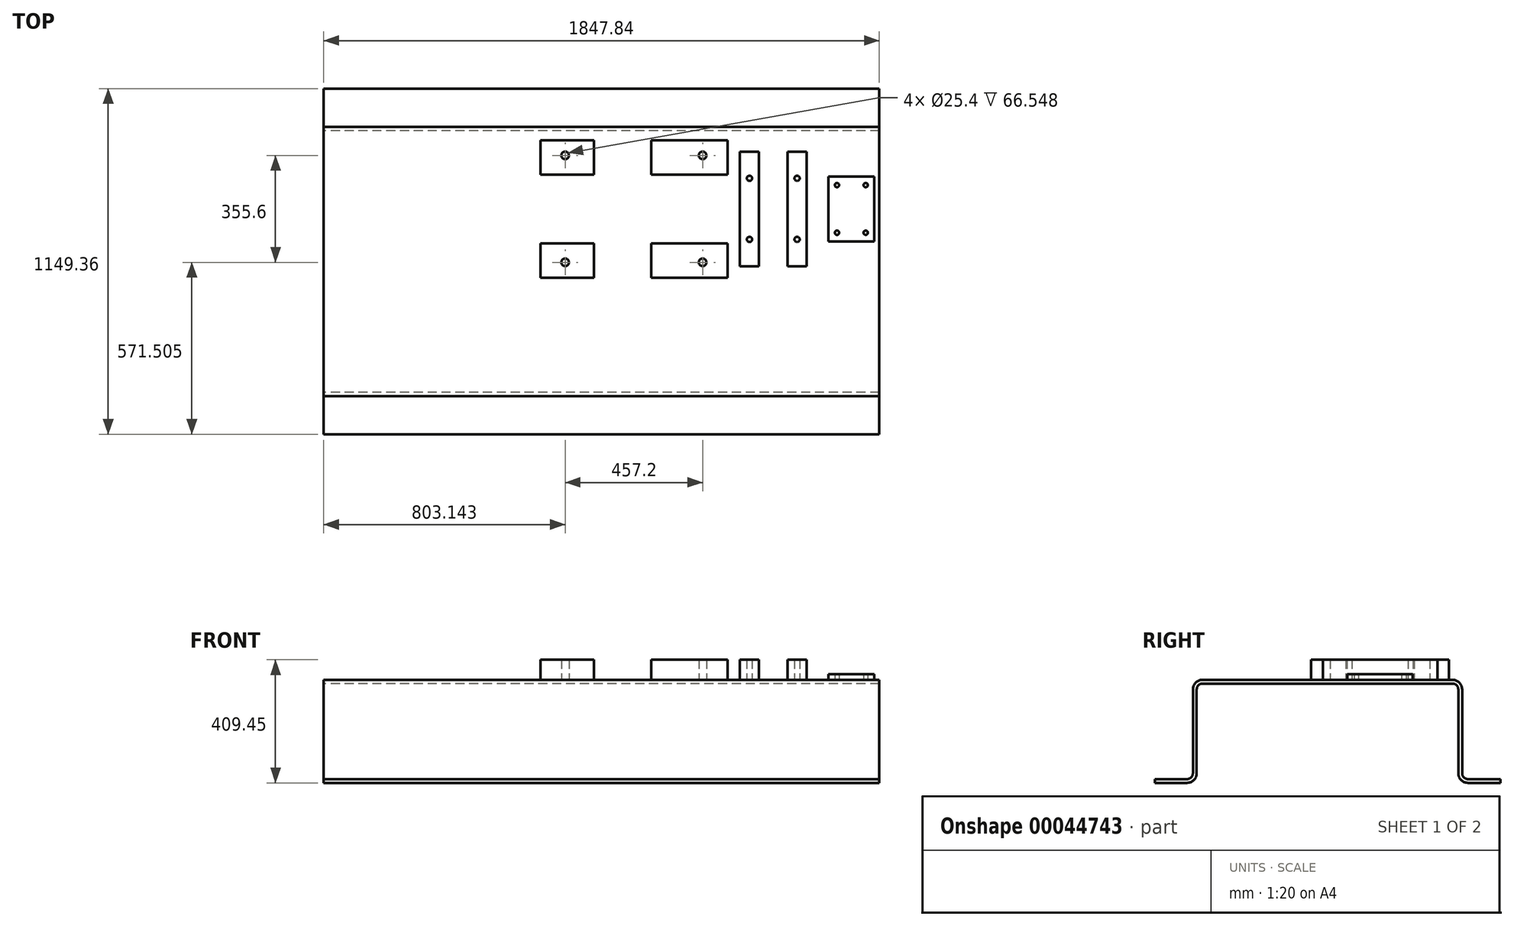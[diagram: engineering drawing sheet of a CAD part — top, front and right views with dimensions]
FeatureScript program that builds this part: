
annotation { "Feature Type Name" : "Feature", "Feature Type Description" : "" }
export const myFeature = defineFeature(function(context is Context, id is Id, definition is map)
    precondition{}
    {
        {
            var Q0;
            Q0=qCreatedBy(makeId("Right.planeOp"),FACE);
            var sketch = newSketch(context, id + "F0", { "sketchPlane" : qUnion([Q0])});
            skLineSegment(sketch, "E0.rect.bottom", {"start": v(-415.92, 171.45) * mm, "end": v(415.93, 171.45) * mm});
            skLineSegment(sketch, "E0.rect.top", {"start": v(-574.68, -171.45) * mm, "end": v(-466.73, -171.45) * mm});
            skLineSegment(sketch, "E0.rect.left", {"start": v(-447.68, 139.7) * mm, "end": v(-447.68, -139.7) * mm});
            skLineSegment(sketch, "E0.rect.right", {"start": v(447.68, 139.7) * mm, "end": v(447.68, -139.7) * mm});
            skPoint(sketch, "E0.rect.middle", {"position": v(0, 0) * mm});
            skLineSegment(sketch, "E1.0", {"start": v(-415.93, 158.75) * mm, "end": v(415.92, 158.75) * mm});
            skLineSegment(sketch, "E1.1", {"start": v(-434.98, 139.7) * mm, "end": v(-434.98, -139.7) * mm});
            skLineSegment(sketch, "E1.2", {"start": v(-574.68, -158.75) * mm, "end": v(-466.73, -158.75) * mm});
            skLineSegment(sketch, "E1.3", {"start": v(434.97, 139.7) * mm, "end": v(434.97, -139.7) * mm});
            skLineSegment(sketch, "E2.0", {"start": v(-574.68, -158.75) * mm, "end": v(-574.68, -171.45) * mm});
            skPoint(sketch, "E3.orphan", {"position": v(-447.68, -171.45) * mm});
            skLineSegment(sketch, "E4", {"start": v(0, 0) * mm, "end": v(0, 367.06) * mm, "construction": true});
            skLineSegment(sketch, "E5.MirrorCS", {"start": v(574.68, -158.75) * mm, "end": v(574.68, -171.45) * mm});
            skLineSegment(sketch, "E6.MirrorCS", {"start": v(574.68, -158.75) * mm, "end": v(466.73, -158.75) * mm});
            skPoint(sketch, "E7.MirrorP", {"position": v(447.68, -171.45) * mm});
            skLineSegment(sketch, "E8.MirrorCS", {"start": v(574.68, -171.45) * mm, "end": v(466.73, -171.45) * mm});
            skPoint(sketch, "E9.visualSharp", {"position": v(447.68, -158.75) * mm});
            skArc(sketch, "E9.filletArc", {"start": v(447.68, -139.7) * mm, "mid": v(453.25, -153.17) * mm, "end": v(466.73, -158.75) * mm});
            skPoint(sketch, "E10.visualSharp", {"position": v(434.98, 158.75) * mm});
            skArc(sketch, "E10.filletArc", {"start": v(434.97, 139.7) * mm, "mid": v(429.4, 153.17) * mm, "end": v(415.92, 158.75) * mm});
            skPoint(sketch, "E11.visualSharp", {"position": v(-434.98, 158.75) * mm});
            skArc(sketch, "E11.filletArc", {"start": v(-415.93, 158.75) * mm, "mid": v(-429.4, 153.17) * mm, "end": v(-434.98, 139.7) * mm});
            skPoint(sketch, "E12.visualSharp", {"position": v(-447.68, -158.75) * mm});
            skArc(sketch, "E12.filletArc", {"start": v(-466.73, -158.75) * mm, "mid": v(-453.25, -153.17) * mm, "end": v(-447.68, -139.7) * mm});
            skPoint(sketch, "E13.visualSharp", {"position": v(-434.98, -171.45) * mm});
            skArc(sketch, "E13.filletArc", {"start": v(-466.73, -171.45) * mm, "mid": v(-444.27, -162.15) * mm, "end": v(-434.98, -139.7) * mm});
            skPoint(sketch, "E14.visualSharp", {"position": v(-447.68, 171.45) * mm});
            skArc(sketch, "E14.filletArc", {"start": v(-415.92, 171.45) * mm, "mid": v(-438.38, 162.15) * mm, "end": v(-447.67, 139.7) * mm});
            skPoint(sketch, "E15.visualSharp", {"position": v(447.68, 171.45) * mm});
            skArc(sketch, "E15.filletArc", {"start": v(447.68, 139.7) * mm, "mid": v(438.38, 162.15) * mm, "end": v(415.93, 171.45) * mm});
            skPoint(sketch, "E16.visualSharp", {"position": v(434.97, -171.45) * mm});
            skArc(sketch, "E16.filletArc", {"start": v(434.98, -139.7) * mm, "mid": v(444.27, -162.15) * mm, "end": v(466.73, -171.45) * mm});
            skSolve(sketch);
        }
        {
            var Q0;
            Q0 = qSketchRegion(id + "F0", true);
            extrude(context, id + "F1", {"entities" : qUnion([Q0]), "endBound" : BoundingType.SYMMETRIC, "depth" : 1847.85 * mm});
        }
        {
            var Q0;
            Q0=makeQuery(id+"F1.opExtrude","SWEPT_FACE",FACE,{"disambiguationData":[OSD([sQuery(id+"F0.wireOp",EDGE,"E0.rect.bottom")])]});
            var sketch = newSketch(context, id + "F2", { "sketchPlane" : qUnion([Q0])});
            skLineSegment(sketch, "E17.0", {"start": v(-923.93, -415.92) * mm, "end": v(-923.93, 415.93) * mm, "construction": true});
            skLineSegment(sketch, "E18.0", {"start": v(-669.93, -415.92) * mm, "end": v(-669.93, 415.93) * mm, "construction": true});
            skLineSegment(sketch, "E19.0", {"start": v(107.82, -415.92) * mm, "end": v(107.82, 415.93) * mm, "construction": true});
            skLineSegment(sketch, "E20.0", {"start": v(571.37, -415.92) * mm, "end": v(571.37, 415.93) * mm, "construction": true});
            skLineSegment(sketch, "E21.0", {"start": v(830.96, -415.92) * mm, "end": v(830.96, 415.93) * mm, "construction": true});
            skLineSegment(sketch, "E22.0", {"start": v(923.93, -574.68) * mm, "end": v(-923.93, -574.68) * mm, "construction": true});
            skLineSegment(sketch, "E23.0", {"start": v(923.93, -206.38) * mm, "end": v(-923.93, -206.38) * mm, "construction": true});
            skLineSegment(sketch, "E24.0", {"start": v(923.93, 174.63) * mm, "end": v(-923.93, 174.63) * mm, "construction": true});
            skLineSegment(sketch, "E25.0", {"start": v(907.16, 282.58) * mm, "end": v(754.76, 282.58) * mm});
            skLineSegment(sketch, "E26.MirrorCS", {"start": v(907.16, 66.68) * mm, "end": v(754.76, 66.68) * mm});
            skPoint(sketch, "E27.orphan", {"position": v(907.16, 415.93) * mm});
            skPoint(sketch, "E28.orphan", {"position": v(754.76, 415.93) * mm});
            skLineSegment(sketch, "E29.trimOffspring", {"start": v(754.76, 66.68) * mm, "end": v(754.76, 282.57) * mm});
            skLineSegment(sketch, "E30.trimOffspring", {"start": v(907.16, 66.68) * mm, "end": v(907.16, 282.57) * mm});
            skPoint(sketch, "E31.orphan", {"position": v(923.93, 66.68) * mm});
            skPoint(sketch, "E32.orphan", {"position": v(923.93, 282.58) * mm});
            skLineSegment(sketch, "E33.0", {"start": v(783.2, -415.92) * mm, "end": v(783.2, 415.93) * mm, "construction": true});
            skLineSegment(sketch, "E34.0", {"start": v(923.93, 253.87) * mm, "end": v(-923.93, 253.87) * mm, "construction": true});
            skCircle(sketch, "E35", {"center": v(783.2, 253.87) * mm, "radius": 7.14 * mm});
            skCircle(sketch, "E36.MirrorC", {"center": v(878.71, 253.87) * mm, "radius": 7.14 * mm});
            skCircle(sketch, "E37.MirrorC", {"center": v(783.2, 95.38) * mm, "radius": 7.14 * mm});
            skCircle(sketch, "E38.MirrorC", {"center": v(878.71, 95.38) * mm, "radius": 7.14 * mm});
            skSolve(sketch);
        }
        {
            var Q0;
            Q0 = qSketchRegion(id + "F2", true);
            extrude(context, id + "F3", {"entities" : qUnion([Q0]), "operationType" : NewBodyOperationType.ADD, "depth" : 19.05 * mm});
        }
        {
            var Q0;
            Q0=makeQuery(id+"F2.imprint","IMPRINT",FACE,{"disambiguationData":[TD([[makeQuery(id+"F2.imprint","IMPRINT",EDGE,{"derivedFrom":sQuery(id+"F2.wireOp",EDGE,"E25.0")}),-1.0]])]});
            var sketch = newSketch(context, id + "F4", { "sketchPlane" : qUnion([Q0])});
            skLineSegment(sketch, "E39.0", {"start": v(523.62, -15.88) * mm, "end": v(523.62, 365.13) * mm});
            skLineSegment(sketch, "E40.0", {"start": v(460.12, -15.88) * mm, "end": v(460.12, 365.13) * mm});
            skLineSegment(sketch, "E41.0", {"start": v(523.62, -15.88) * mm, "end": v(460.12, -15.88) * mm});
            skLineSegment(sketch, "E42.0", {"start": v(523.62, 365.13) * mm, "end": v(460.12, 365.13) * mm});
            skLineSegment(sketch, "E43.0", {"start": v(492.13, -415.92) * mm, "end": v(492.13, 415.93) * mm, "construction": true});
            skLineSegment(sketch, "E44.0", {"start": v(923.93, 73.03) * mm, "end": v(-923.93, 73.03) * mm, "construction": true});
            skCircle(sketch, "E45", {"center": v(492.13, 73.03) * mm, "radius": 8.73 * mm});
            skCircle(sketch, "E46.MirrorC", {"center": v(492.13, 276.23) * mm, "radius": 8.73 * mm});
            skCircle(sketch, "E47.MirrorC", {"center": v(650.62, 73.03) * mm, "radius": 8.73 * mm});
            skCircle(sketch, "E48.MirrorC", {"center": v(650.62, 276.23) * mm, "radius": 8.73 * mm});
            skLineSegment(sketch, "E49.MirrorCS", {"start": v(619.12, -15.88) * mm, "end": v(682.62, -15.88) * mm});
            skLineSegment(sketch, "E50.MirrorCS", {"start": v(619.12, -15.88) * mm, "end": v(619.12, 365.13) * mm});
            skLineSegment(sketch, "E51.MirrorCS", {"start": v(682.62, -15.88) * mm, "end": v(682.62, 365.13) * mm});
            skLineSegment(sketch, "E52.MirrorCS", {"start": v(619.12, 365.13) * mm, "end": v(682.62, 365.13) * mm});
            skSolve(sketch);
        }
        {
            var Q0;
            Q0 = qSketchRegion(id + "F4", true);
            extrude(context, id + "F5", {"entities" : qUnion([Q0]), "operationType" : NewBodyOperationType.ADD, "depth" : 66.55 * mm});
        }
        {
            var Q0;
            Q0=makeQuery(id+"F2.imprint","IMPRINT",FACE,{"disambiguationData":[TD([[makeQuery(id+"F2.imprint","IMPRINT",EDGE,{"derivedFrom":sQuery(id+"F2.wireOp",EDGE,"E25.0")}),-1.0]])]});
            var sketch = newSketch(context, id + "F6", { "sketchPlane" : qUnion([Q0])});
            skLineSegment(sketch, "E53.0", {"start": v(-25.53, -53.97) * mm, "end": v(-25.53, 60.33) * mm});
            skLineSegment(sketch, "E54.0", {"start": v(-203.33, -53.97) * mm, "end": v(-203.33, 60.33) * mm});
            skLineSegment(sketch, "E55.0", {"start": v(164.97, -53.97) * mm, "end": v(164.97, 60.33) * mm});
            skLineSegment(sketch, "E56.0", {"start": v(418.97, -53.97) * mm, "end": v(418.97, 60.33) * mm});
            skLineSegment(sketch, "E57.0", {"start": v(418.97, 60.33) * mm, "end": v(164.97, 60.33) * mm});
            skLineSegment(sketch, "E58.0", {"start": v(418.97, -53.97) * mm, "end": v(164.97, -53.97) * mm});
            skLineSegment(sketch, "E59.trimOffspring", {"start": v(-25.53, 60.33) * mm, "end": v(-203.33, 60.33) * mm});
            skLineSegment(sketch, "E60.trimOffspring", {"start": v(-25.53, -53.97) * mm, "end": v(-203.33, -53.97) * mm});
            skLineSegment(sketch, "E61.0", {"start": v(-120.78, -415.92) * mm, "end": v(-120.78, 415.93) * mm, "construction": true});
            skLineSegment(sketch, "E62.0", {"start": v(336.42, -415.92) * mm, "end": v(336.42, 415.93) * mm, "construction": true});
            skLineSegment(sketch, "E63.0", {"start": v(923.93, -3.17) * mm, "end": v(-923.93, -3.17) * mm, "construction": true});
            skCircle(sketch, "E64", {"center": v(-120.78, -3.17) * mm, "radius": 12.7 * mm});
            skCircle(sketch, "E65", {"center": v(336.42, -3.17) * mm, "radius": 12.7 * mm});
            skLineSegment(sketch, "E66.MirrorCS", {"start": v(-25.53, 403.23) * mm, "end": v(-203.33, 403.23) * mm});
            skLineSegment(sketch, "E67.MirrorCS", {"start": v(-25.53, 403.23) * mm, "end": v(-25.53, 288.93) * mm});
            skCircle(sketch, "E68.MirrorC", {"center": v(336.42, 352.43) * mm, "radius": 12.7 * mm});
            skLineSegment(sketch, "E69.MirrorCS", {"start": v(-203.33, 403.23) * mm, "end": v(-203.33, 288.93) * mm});
            skCircle(sketch, "E70.MirrorC", {"center": v(-120.78, 352.43) * mm, "radius": 12.7 * mm});
            skLineSegment(sketch, "E71.MirrorCS", {"start": v(164.97, 403.23) * mm, "end": v(164.97, 288.93) * mm});
            skLineSegment(sketch, "E72.MirrorCS", {"start": v(-25.53, 288.93) * mm, "end": v(-203.33, 288.93) * mm});
            skLineSegment(sketch, "E73.MirrorCS", {"start": v(418.97, 403.23) * mm, "end": v(418.97, 288.93) * mm});
            skLineSegment(sketch, "E74.MirrorCS", {"start": v(418.97, 288.93) * mm, "end": v(164.97, 288.93) * mm});
            skLineSegment(sketch, "E75.MirrorCS", {"start": v(418.97, 403.23) * mm, "end": v(164.97, 403.23) * mm});
            skSolve(sketch);
        }
        {
            var Q0;
            Q0 = qSketchRegion(id + "F6", true);
            extrude(context, id + "F7", {"entities" : qUnion([Q0]), "operationType" : NewBodyOperationType.ADD, "depth" : 66.55 * mm});
        }
    });
